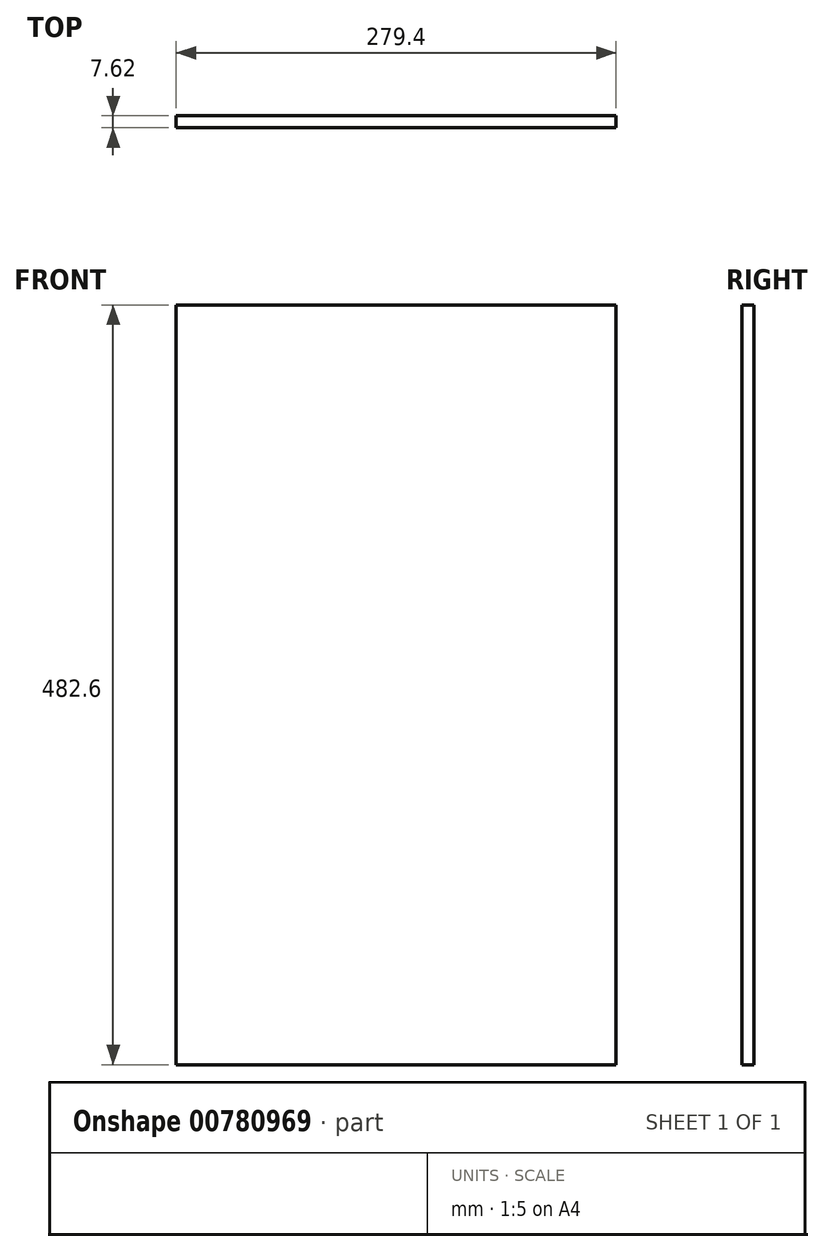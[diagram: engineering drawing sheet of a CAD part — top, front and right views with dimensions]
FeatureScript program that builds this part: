
annotation { "Feature Type Name" : "Feature", "Feature Type Description" : "" }
export const myFeature = defineFeature(function(context is Context, id is Id, definition is map)
    precondition{}
    {
        {
            var Q0;
            Q0=qCreatedBy(makeId("Front.planeOp"),FACE);
            var sketch = newSketch(context, id + "F0", { "sketchPlane" : qUnion([Q0])});
            skLineSegment(sketch, "E0.bottom", {"start": v(-139.7, -241.3) * mm, "end": v(139.7, -241.3) * mm});
            skLineSegment(sketch, "E0.top", {"start": v(-139.7, 241.3) * mm, "end": v(139.7, 241.3) * mm});
            skLineSegment(sketch, "E0.left", {"start": v(-139.7, -241.3) * mm, "end": v(-139.7, 241.3) * mm});
            skLineSegment(sketch, "E0.right", {"start": v(139.7, -241.3) * mm, "end": v(139.7, 241.3) * mm});
            skPoint(sketch, "E0.middle", {"position": v(0, 0) * mm});
            skSolve(sketch);
        }
        {
            var Q0;
            Q0=makeQuery(id+"F0.imprint","IMPRINT",FACE,{"disambiguationData":[TD([[makeQuery(id+"F0.imprint","IMPRINT",EDGE,{"derivedFrom":sQuery(id+"F0.wireOp",EDGE,"E0.bottom")}),1.0]])]});
            extrude(context, id + "F1", {"entities" : qUnion([Q0]), "depth" : 7.62 * mm, "offsetDistance" : 25.4 * mm});
        }
    });
